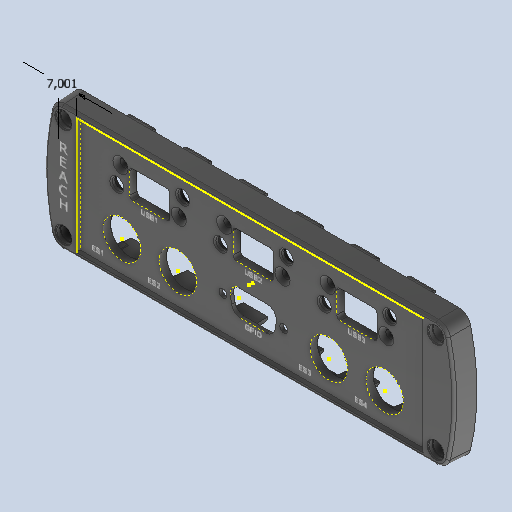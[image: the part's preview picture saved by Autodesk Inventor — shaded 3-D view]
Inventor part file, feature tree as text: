
AUTODESK INVENTOR PART (.ipt)
format: ipt  version: 2022 (Build 260153000, 153)  size: 1,143,296 bytes
history: native  units: mm
features: sketch x11, extrude x9, chamfer x4, fillet x3, plane x2, mirror x1, hole x1, projected_geometry x1, other x1
ambient origin geometry x8: Origin, YZ Plane, XZ Plane, XY Plane, X Axis, Y Axis, Z Axis, Center Point
bodies: Solid1 (feature_tree)
feature tree (33):
  extrude  "Extrusion1"  TaperAngle=0.0deg  [1 undecoded]
  fillet  "Fillet1"  Radius=6.9mm
  plane  "Work Plane1"
  extrude  "Extrusion4"  [1 undecoded]
  chamfer  "Chamfer2"  [1 undecoded]
  mirror  "Mirror1"
  plane  "Work Plane2"
  extrude  "Extrusion6"  Depth=0.2mm
  extrude  "Extrusion7"  Depth=3.3mm
  chamfer  "Chamfer3"  Distance=5.23mm
  extrude  "Extrusion9"  Depth=1.0mm
  fillet  "Fillet3"  [1 undecoded]
  hole  "Hole1"  [1 undecoded]
  extrude  "Extrusion10"  Depth=1.0mm
  extrude  "Extrusion11"  Depth=1.0mm
  extrude  "Extrusion12"  Depth=1.0mm
  fillet  "Fillet4"  Radius=10.075mm
  chamfer  "Chamfer4"  Distance=42.584mm
  chamfer  "Chamfer5"  Distance=7.0mm
  extrude  "Extrusion13"  Depth=10.0mm TaperAngle=0.0deg
  sketch  "Sketch20"  dims[d54=10.46mm d56=3.3mm]
  sketch  "Sketch21"  dims[d57=12.495mm d58=5.23mm d59=4.77mm d60=0.0mm d61=0.0mm d63=3.72mm d64=9.51mm d65=4.85mm d66=4.85mm d67=27.0mm d68=9.0mm d69=3.3mm d70=3.3mm d71=24.0mm d72=16.55mm d73=11.55mm d74=6.35mm d75=1.85mm d76=5.225mm d77=6.9mm d78=10.075mm d79=10.075mm d80=42.584mm d82=7.0mm d83=10.0mm d84=0.0mm d85=0.5mm d86=2.0mm d87=45.0deg d101=10.075mm d102=4.85mm d103=4.85mm d104=27.0mm d105=9.0mm d106=3.3mm d107=3.3mm d108=24.0mm d109=16.55mm d110=11.55mm d111=6.35mm d112=1.85mm d113=5.225mm d114=10.075mm d115=12.0mm d116=6.9mm d117=42.584mm d118=7.0mm d119=7.0mm d122=12.0mm d123=41.0mm d124=2.0mm d125=0.0mm d126=2.0mm d127=3.25mm d128=6.0mm d129=6.25mm d130=2.0mm d131=90.0deg d132=8.0mm d133=20.594885mm d134=10.0mm d135=0.0mm d136=10.0mm d137=0.0mm d138=0.2mm d139=0.0mm d140=3.0mm d141=0.2mm d142=2.0mm d143=45.0deg d144=0.2mm d145=2.0mm d146=45.0deg d147=10.0mm d148=0.0mm d149=8.0mm d150=12.5mm d151=8.0mm d152=12.5mm d153=12.5mm d154=8.0mm d155=8.0mm d156=12.5mm d157=4.5mm d160=4.5mm d161=1.0mm d164=1.0mm d165=1.0mm d166=2.25mm d167=28.699852mm d169=20.0mm d171=42.584mm d172=10.0mm d174=10.0mm d176=7.0mm d177=7.0mm d178=7.0mm d179=1.0mm d180=4.5mm d181=7.001437mm]
  sketch  "Sketch1"  dims[d3=9.0mm d15=0.0mm d16=0.0mm d21=6.9mm]
  sketch  "Sketch5"  dims[d23=1.35mm d26=-1.5mm]
  sketch  "Sketch8"  dims[d40=15.4mm]
  sketch  "Sketch14"  dims[d41=11.5mm]
  sketch  "Sketch15"  dims[d42=54.0mm]
  sketch  "Sketch16"  dims[d43=15.4mm]
  projected_geometry  "Projected Loop5"
  sketch  "Sketch17"  dims[d44=0.0mm]
  sketch  "Sketch18"  dims[d45=31.0mm d46=0.0mm d47=0.0mm]
  sketch  "Sketch19"  dims[d48=0.2mm d49=2.0mm d50=45.0deg d53=1.745329mm]
  other  "1009799_3D"
note: 5 required parameter values undecoded (feature->parameter linkage not recoverable at this tier; creation-order binding heuristic only, values carry confidence <= 0.55)
